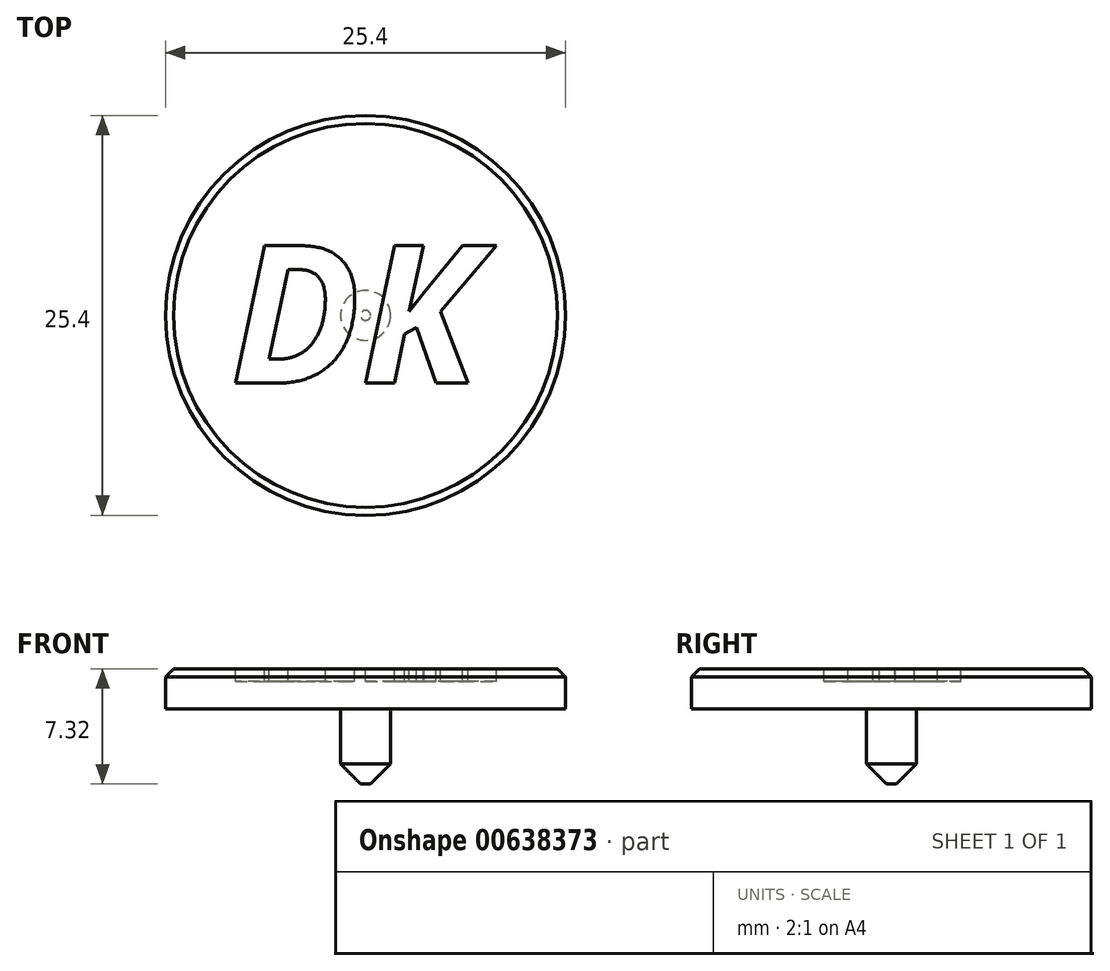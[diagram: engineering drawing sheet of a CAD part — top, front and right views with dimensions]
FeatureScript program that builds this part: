
annotation { "Feature Type Name" : "Feature", "Feature Type Description" : "" }
export const myFeature = defineFeature(function(context is Context, id is Id, definition is map)
    precondition{}
    {
        {
            var Q0;
            Q0=qCreatedBy(makeId("Top.planeOp"),FACE);
            var sketch = newSketch(context, id + "F0", { "sketchPlane" : qUnion([Q0])});
            skCircle(sketch, "E0", {"center": v(0, 0) * mm, "radius": 12.7 * mm});
            skLineSegment(sketch, "E1", {"start": v(-12.7, 0) * mm, "end": v(-12.7, 10.24) * mm, "construction": true});
            skLineSegment(sketch, "E2", {"start": v(12.7, 0) * mm, "end": v(12.7, 10.24) * mm, "construction": true});
            skSolve(sketch);
        }
        {
            var Q0;
            Q0=makeQuery(id+"F0.imprint","IMPRINT",FACE,{"disambiguationData":[TD([[makeQuery(id+"F0.imprint","IMPRINT",EDGE,{"derivedFrom":sQuery(id+"F0.wireOp",EDGE,"E0")}),1.0]])]});
            extrude(context, id + "F1", {"entities" : qUnion([Q0]), "depth" : 2.54 * mm, "offsetDistance" : 25.4 * mm});
        }
        {
            var Q0;
            Q0=makeQuery(id+"F1.opExtrude","CAP_EDGE",EDGE,{"disambiguationData":[OSD([sQuery(id+"F0.wireOp",EDGE,"E0")])],"isStart":false});
            chamfer(context, id + "F2", {"entities" : qUnion([Q0]), "width" : 0.5 * mm, "tangentPropagation" : true});
        }
        {
            var Q0;
            Q0=makeQuery(id+"F1.opExtrude","CAP_FACE",FACE,{"disambiguationData":[OSD([sQuery(id+"F0.wireOp",EDGE,"E0")])],"isStart":true});
            var sketch = newSketch(context, id + "F3", { "sketchPlane" : qUnion([Q0])});
            skCircle(sketch, "E3", {"center": v(0, 0) * mm, "radius": 1.59 * mm});
            skSolve(sketch);
        }
        {
            var Q0;
            Q0=makeQuery(id+"F3.imprint","IMPRINT",FACE,{"disambiguationData":[TD([[makeQuery(id+"F3.imprint","IMPRINT",EDGE,{"derivedFrom":sQuery(id+"F3.wireOp",EDGE,"E3")}),1.0]])]});
            extrude(context, id + "F4", {"entities" : qUnion([Q0]), "operationType" : NewBodyOperationType.ADD, "depth" : 4.78 * mm, "offsetDistance" : 25.4 * mm});
        }
        {
            var Q0;
            Q0=makeQuery(id+"F1.opExtrude","CAP_FACE",FACE,{"disambiguationData":[OSD([sQuery(id+"F0.wireOp",EDGE,"E0")])],"isStart":false});
            var sketch = newSketch(context, id + "F5", { "sketchPlane" : qUnion([Q0])});
            skText(sketch, "E4", { "text": "DK", "fontName": "OpenSans-BoldItalic.ttf"});
            const initialGuessF5  = {"E4": [-0.00858, -0.0043, 1, 0, 0.0088]};
            skSetInitialGuess(sketch, initialGuessF5);
            skSolve(sketch);
        }
        {
            var Q0;
            Q0 = qSketchRegion(id + "F5", true);
            extrude(context, id + "F6", {"entities" : qUnion([Q0]), "operationType" : NewBodyOperationType.REMOVE, "oppositeDirection" : true, "depth" : 0.8 * mm, "offsetDistance" : 25.4 * mm});
        }
        {
            var Q0;
            Q0=makeQuery(id+"F4.opExtrude","CAP_EDGE",EDGE,{"disambiguationData":[OSD([sQuery(id+"F3.wireOp",EDGE,"E3")])],"isStart":false});
            chamfer(context, id + "F7", {"entities" : qUnion([Q0]), "width" : 1.27 * mm, "tangentPropagation" : true});
        }
    });
